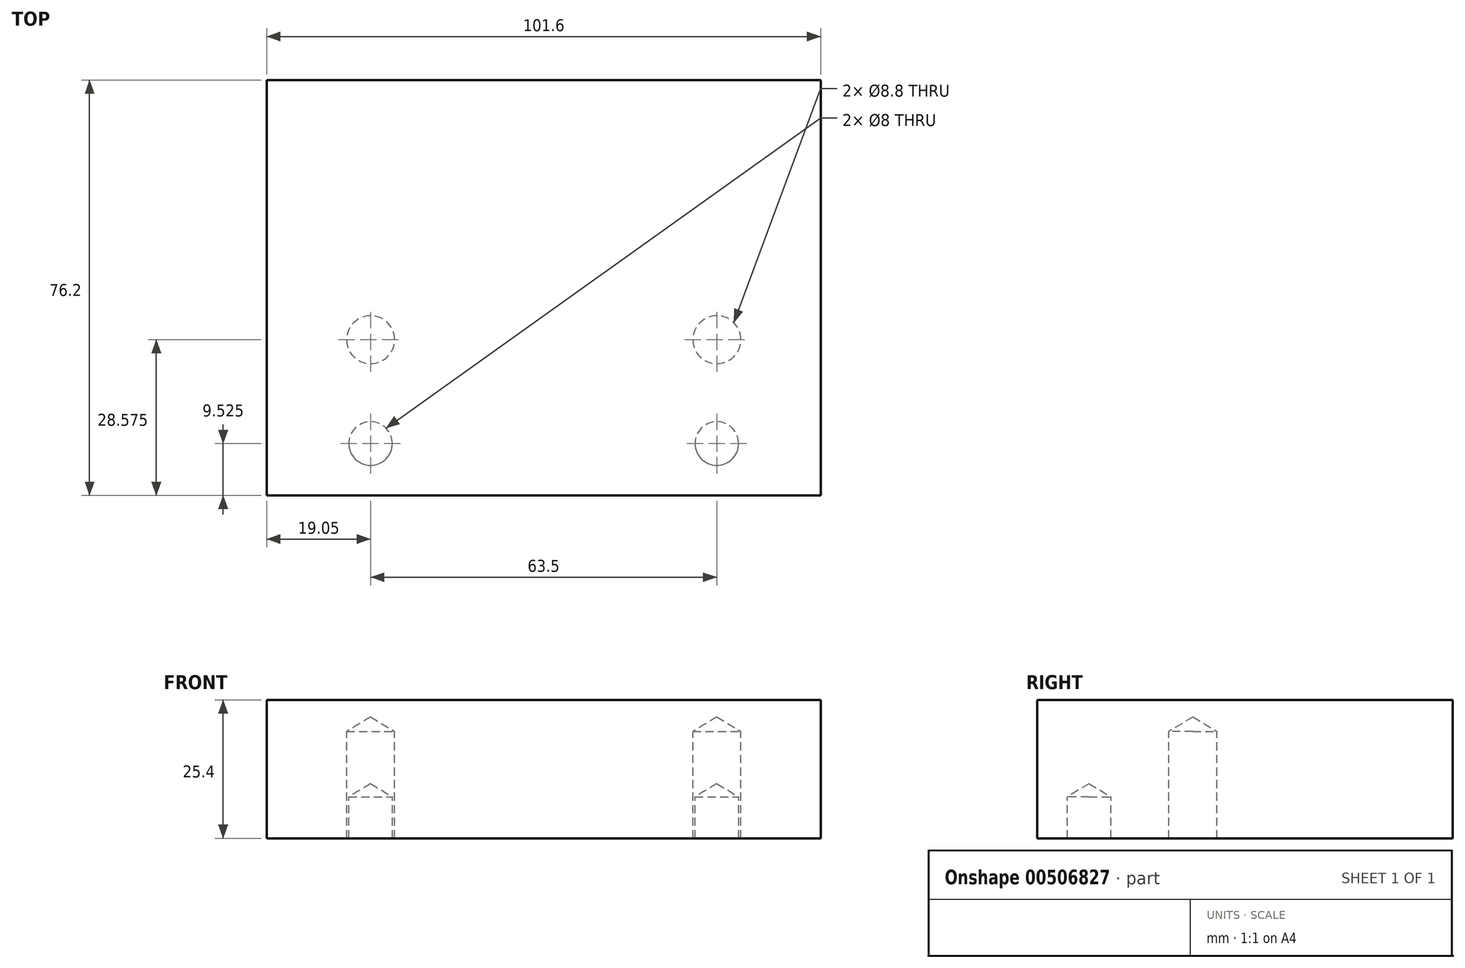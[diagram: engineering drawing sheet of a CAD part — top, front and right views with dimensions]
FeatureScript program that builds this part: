
annotation { "Feature Type Name" : "Feature", "Feature Type Description" : "" }
export const myFeature = defineFeature(function(context is Context, id is Id, definition is map)
    precondition{}
    {
        {
            var Q0;
            Q0=qCreatedBy(makeId("Top.planeOp"),FACE);
            var sketch = newSketch(context, id + "F0", { "sketchPlane" : qUnion([Q0])});
            skLineSegment(sketch, "E0.bottom", {"start": v(0, 0) * mm, "end": v(101.6, 0) * mm});
            skLineSegment(sketch, "E0.top", {"start": v(0, 76.2) * mm, "end": v(101.6, 76.2) * mm});
            skLineSegment(sketch, "E0.left", {"start": v(0, 0) * mm, "end": v(0, 76.2) * mm});
            skLineSegment(sketch, "E0.right", {"start": v(101.6, 0) * mm, "end": v(101.6, 76.2) * mm});
            skLineSegment(sketch, "E1", {"start": v(19.05, 28.58) * mm, "end": v(82.55, 28.58) * mm, "construction": true});
            skLineSegment(sketch, "E2", {"start": v(19.05, 28.58) * mm, "end": v(19.05, 9.53) * mm, "construction": true});
            skLineSegment(sketch, "E3", {"start": v(19.05, 9.52) * mm, "end": v(82.55, 9.52) * mm, "construction": true});
            skLineSegment(sketch, "E4", {"start": v(82.55, 9.52) * mm, "end": v(82.55, 28.58) * mm, "construction": true});
            skPoint(sketch, "E5", {"position": v(82.55, 9.52) * mm});
            skPoint(sketch, "E6", {"position": v(19.05, 9.53) * mm});
            skSolve(sketch);
        }
        {
            var Q0;
            Q0 = qSketchRegion(id + "F0", true);
            extrude(context, id + "F1", {"entities" : qUnion([Q0]), "depth" : 25.4 * mm});
        }
        {
            var Q0;
            Q0=sQuery(id+"F0.wireOp",VERTEX,"E2.start");
            var Q1;
            Q1=sQuery(id+"F0.wireOp",VERTEX,"E4.end");
            var Q2;
            Q2=makeQuery(id+"F1.opExtrude","SWEPT_BODY",BODY,{"disambiguationData":[OSD([sQuery(id+"F0.wireOp",EDGE,"E0.bottom"),sQuery(id+"F0.wireOp",EDGE,"E0.top"),sQuery(id+"F0.wireOp",EDGE,"E0.left"),sQuery(id+"F0.wireOp",EDGE,"E0.right")])]});
            hole(context, id + "F2", {"style" : HoleStyle.SIMPLE, "endStyle" : HoleEndStyle.BLIND, "oppositeDirection" : true, "standardTappedOrClearance" : lookupTablePath({ "standard" : "ISO", "engagement" : "75%", "pitch" : "1.25 mm", "size" : "M10", "type" : "Tapped" }), "standardBlindInLast" : lookupTablePath({ "standard" : "ISO", "engagement" : "75%", "pitch" : "1.25 mm", "size" : "M10", "type" : "Tapped" }), "holeDiameter" : 8.8 * mm, "showTappedDepth" : true, "holeDepth" : 19.62 * mm, "isTappedThrough" : true, "tappedDepth" : 15.88 * mm, "tapClearance" : 3, "locations" : qUnion([Q0, Q1]), "scope" : qUnion([Q2]), "majorDiameter" : 10 * mm});
        }
        {
            var Q0;
            Q0=sQuery(id+"F0.wireOp",VERTEX,"E5");
            var Q1;
            Q1=sQuery(id+"F0.wireOp",VERTEX,"E6");
            var Q2;
            Q2=makeQuery(id+"F1.opExtrude","SWEPT_BODY",BODY,{"disambiguationData":[OSD([sQuery(id+"F0.wireOp",EDGE,"E0.bottom"),sQuery(id+"F0.wireOp",EDGE,"E0.top"),sQuery(id+"F0.wireOp",EDGE,"E0.left"),sQuery(id+"F0.wireOp",EDGE,"E0.right")])]});
            hole(context, id + "F3", {"style" : HoleStyle.SIMPLE, "endStyle" : HoleEndStyle.BLIND, "oppositeDirection" : true, "standardTappedOrClearance" : lookupTablePath({ "standard" : "ISO", "size" : "8", "type" : "Drilled" }), "standardBlindInLast" : lookupTablePath({ "standard" : "ISO", "size" : "8", "type" : "Drilled" }), "holeDiameter" : 8 * mm, "holeDepth" : 7.62 * mm, "isTappedThrough" : true, "tappedDepth" : 15.88 * mm, "tapClearance" : 3, "locations" : qUnion([Q0, Q1]), "scope" : qUnion([Q2])});
        }
    });
